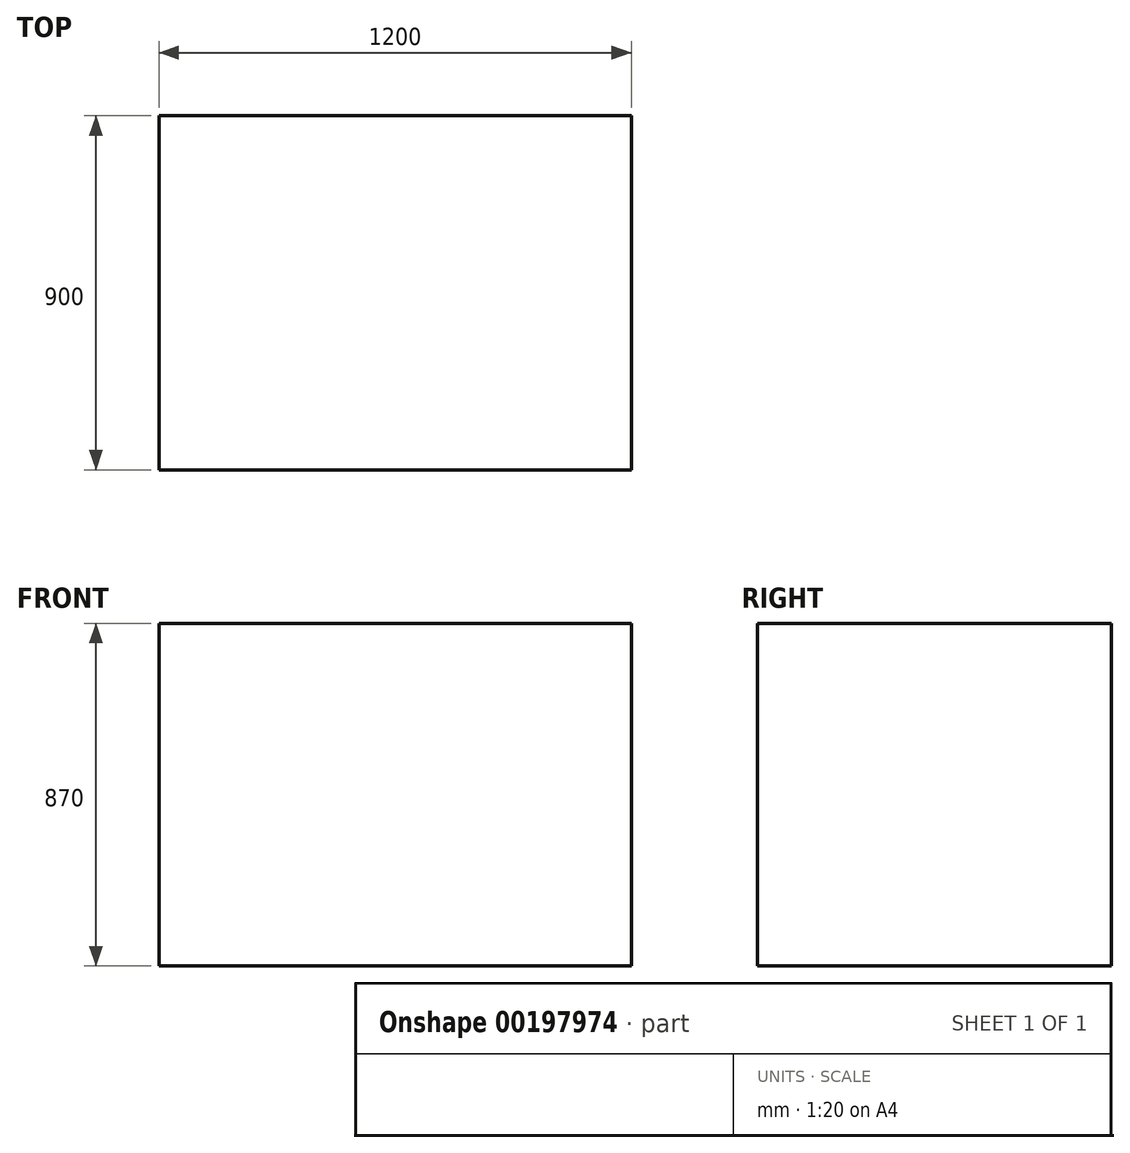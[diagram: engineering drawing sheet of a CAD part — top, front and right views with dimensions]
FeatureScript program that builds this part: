
annotation { "Feature Type Name" : "Feature", "Feature Type Description" : "" }
export const myFeature = defineFeature(function(context is Context, id is Id, definition is map)
    precondition{}
    {
        {
            var Q0;
            Q0=qCreatedBy(makeId("Top.planeOp"),FACE);
            var sketch = newSketch(context, id + "F0", { "sketchPlane" : qUnion([Q0])});
            skLineSegment(sketch, "E0.bottom", {"start": v(-1200, 900) * mm, "end": v(0, 900) * mm});
            skLineSegment(sketch, "E0.top", {"start": v(-1200, 0) * mm, "end": v(0, 0) * mm});
            skLineSegment(sketch, "E0.left", {"start": v(-1200, 900) * mm, "end": v(-1200, 0) * mm});
            skLineSegment(sketch, "E0.right", {"start": v(0, 900) * mm, "end": v(0, 0) * mm});
            skSolve(sketch);
        }
        {
            var Q0;
            Q0=makeQuery(id+"F0.imprint","IMPRINT",FACE,{"disambiguationData":[TD([[makeQuery(id+"F0.imprint","IMPRINT",EDGE,{"derivedFrom":sQuery(id+"F0.wireOp",EDGE,"E0.bottom")}),-1.0]])]});
            extrude(context, id + "F1", {"entities" : qUnion([Q0]), "depth" : 870 * mm});
        }
    });
